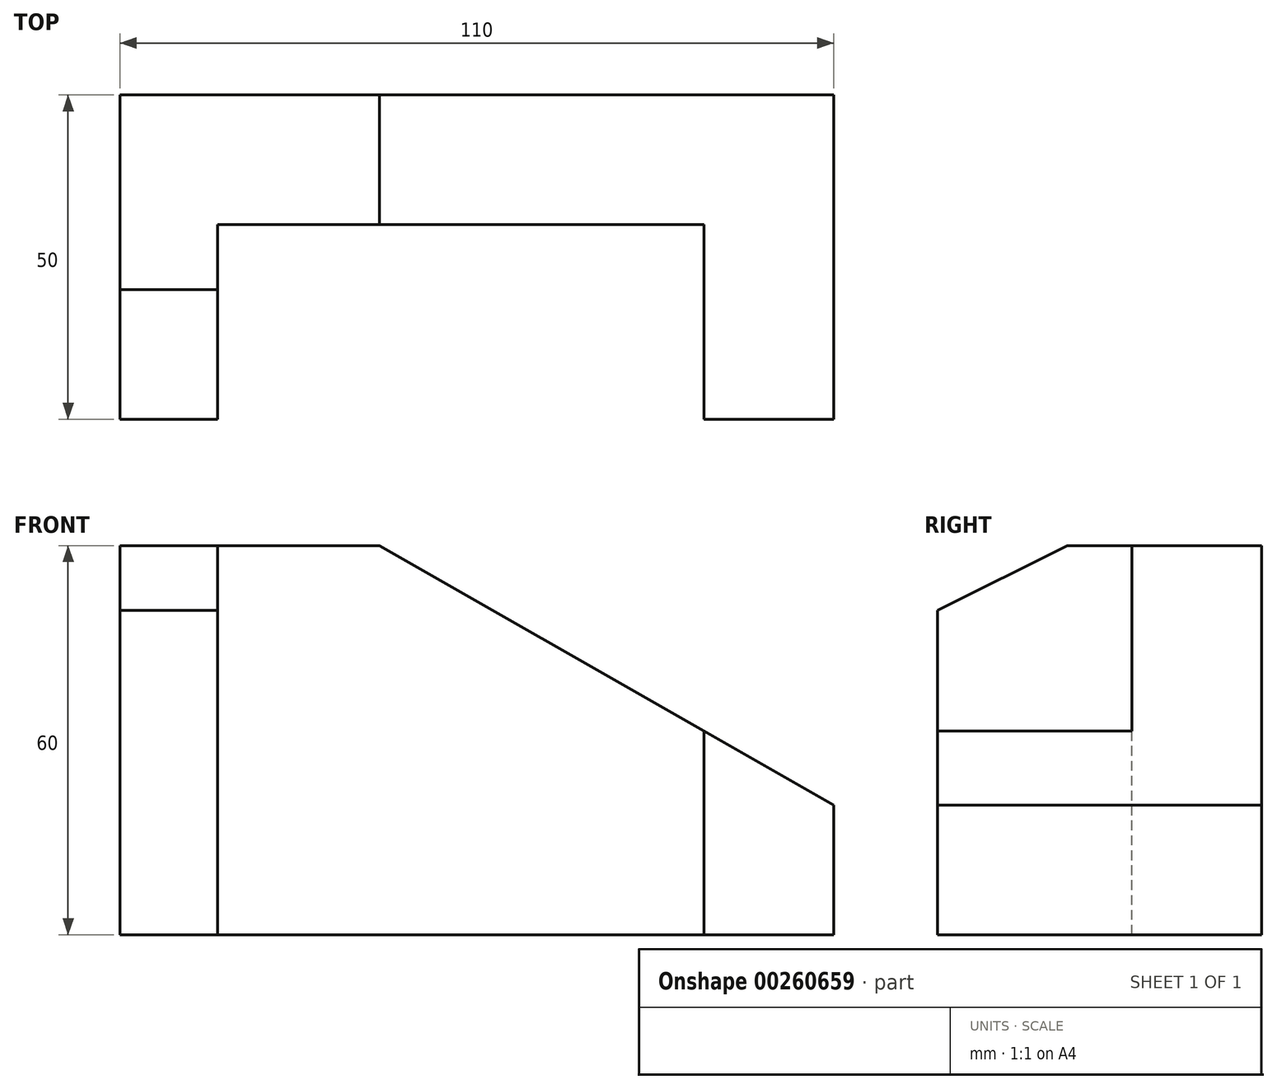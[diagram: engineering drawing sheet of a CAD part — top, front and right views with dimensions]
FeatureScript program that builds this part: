
annotation { "Feature Type Name" : "Feature", "Feature Type Description" : "" }
export const myFeature = defineFeature(function(context is Context, id is Id, definition is map)
    precondition{}
    {
        {
            assignVariable(context, id + "F0", {"name" : "B", "anyValue" : 60});
        }
        {
            assignVariable(context, id + "F1", {"name" : "C", "anyValue" : 50});
        }
        {
            var Q0;
            Q0=qCreatedBy(makeId("Top.planeOp"),FACE);
            var sketch = newSketch(context, id + "F2", { "sketchPlane" : qUnion([Q0])});
            skLineSegment(sketch, "E0.bottom", {"start": v(55, -25) * mm, "end": v(-55, -25) * mm});
            skLineSegment(sketch, "E0.top", {"start": v(55, 25) * mm, "end": v(-55, 25) * mm});
            skLineSegment(sketch, "E0.left", {"start": v(55, -25) * mm, "end": v(55, 25) * mm});
            skLineSegment(sketch, "E0.right", {"start": v(-55, -25) * mm, "end": v(-55, 25) * mm});
            skPoint(sketch, "E0.middle", {"position": v(0, 0) * mm});
            skSolve(sketch);
        }
        {
            var Q0;
            Q0 = qSketchRegion(id + "F2", true);
            extrude(context, id + "F3", {"entities" : qUnion([Q0]), "depth" : (getVariable(context, 'B')) * mm});
        }
        {
            var Q0;
            Q0=makeQuery(id+"F3.opExtrude","SWEPT_FACE",FACE,{"disambiguationData":[OSD([sQuery(id+"F2.wireOp",EDGE,"E0.bottom")])]});
            var sketch = newSketch(context, id + "F4", { "sketchPlane" : qUnion([Q0])});
            skLineSegment(sketch, "E1.bottom", {"start": v(-40, 0) * mm, "end": v(35, 0) * mm});
            skLineSegment(sketch, "E1.top", {"start": v(-40, 60) * mm, "end": v(35, 60) * mm});
            skLineSegment(sketch, "E1.left", {"start": v(-40, 0) * mm, "end": v(-40, 60) * mm});
            skLineSegment(sketch, "E1.right", {"start": v(35, 0) * mm, "end": v(35, 60) * mm});
            skPoint(sketch, "E1.middle", {"position": v(0, 30) * mm});
            skSolve(sketch);
        }
        {
            var Q0;
            Q0 = qSketchRegion(id + "F4", true);
            extrude(context, id + "F5", {"entities" : qUnion([Q0]), "operationType" : NewBodyOperationType.REMOVE, "oppositeDirection" : true, "depth" : 30 * mm});
        }
        {
            var Q0;
            Q0=makeQuery(id+"F3.opExtrude","SWEPT_FACE",FACE,{"disambiguationData":[OSD([sQuery(id+"F2.wireOp",EDGE,"E0.top")])]});
            var sketch = newSketch(context, id + "F6", { "sketchPlane" : qUnion([Q0])});
            skLineSegment(sketch, "E2", {"start": v(-55, 60) * mm, "end": v(15, 60) * mm});
            skLineSegment(sketch, "E3", {"start": v(15, 60) * mm, "end": v(-55, 20) * mm});
            skLineSegment(sketch, "E4", {"start": v(-55, 20) * mm, "end": v(-55, 60) * mm});
            skSolve(sketch);
        }
        {
            var Q0;
            Q0 = qSketchRegion(id + "F6", true);
            extrude(context, id + "F7", {"entities" : qUnion([Q0]), "operationType" : NewBodyOperationType.REMOVE, "oppositeDirection" : true, "depth" : (getVariable(context, 'C')) * mm});
        }
        {
            var Q0;
            Q0=makeQuery(id+"F3.opExtrude","SWEPT_FACE",FACE,{"disambiguationData":[OSD([sQuery(id+"F2.wireOp",EDGE,"E0.right")])]});
            var sketch = newSketch(context, id + "F8", { "sketchPlane" : qUnion([Q0])});
            skLineSegment(sketch, "E5", {"start": v(25, 60) * mm, "end": v(5, 60) * mm});
            skLineSegment(sketch, "E6", {"start": v(5, 60) * mm, "end": v(25, 50) * mm});
            skLineSegment(sketch, "E7", {"start": v(25, 50) * mm, "end": v(25, 60) * mm});
            skSolve(sketch);
        }
        {
            var Q0;
            Q0=makeQuery(id+"F8.imprint","IMPRINT",FACE,{"disambiguationData":[TD([[makeQuery(id+"F8.imprint","IMPRINT",EDGE,{"derivedFrom":sQuery(id+"F8.wireOp",EDGE,"E5")}),1.0]])]});
            extrude(context, id + "F9", {"entities" : qUnion([Q0]), "operationType" : NewBodyOperationType.REMOVE, "oppositeDirection" : true, "depth" : 15 * mm});
        }
    });
